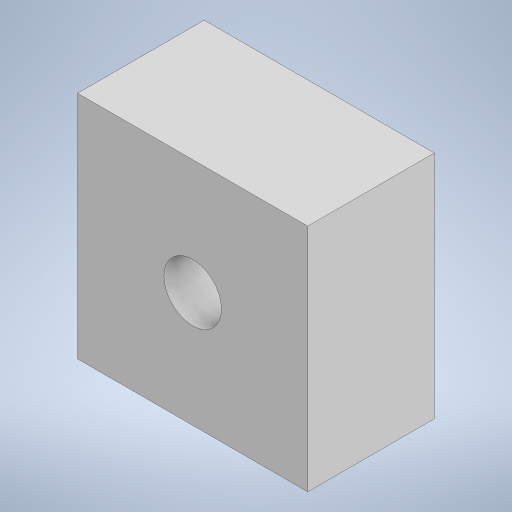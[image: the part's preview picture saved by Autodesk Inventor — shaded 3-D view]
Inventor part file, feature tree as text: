
AUTODESK INVENTOR PART (.ipt)
format: ipt  version: 2023 (Build 270158000, 158)  size: 198,144 bytes
history: native  units: in
note: dims shown in document units (in); Inventor stores cm internally (conversion verified against a paired STEP export)
features: extrude x2, sketch x2
ambient origin geometry x8: Origin, YZ Plane, XZ Plane, XY Plane, X Axis, Y Axis, Z Axis, Center Point
bodies: Body1 (feature_tree)
feature tree (4):
  extrude  "Extrusion2"  Depth=0.7874in
  extrude  "Extrusion3"  Depth=0.3937in
  sketch  "Sketch1"  dims[d0=0.7874in d1=0.7874in]
  sketch  "Sketch3"  dims[d5=0.3937in d6=0.3937in d7=0.1969in d8=0.1969in d9=0.0in d10=0.3543in d11=0.2362in d12=0.0in]
